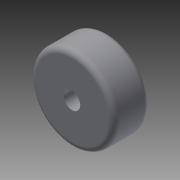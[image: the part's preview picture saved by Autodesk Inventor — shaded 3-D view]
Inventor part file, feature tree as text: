
AUTODESK INVENTOR PART (.ipt)
format: ipt  version: 2013 (Build 170138000, 138)  size: 110,592 bytes
history: native  units: in
note: dims shown in document units (in); Inventor stores cm internally (conversion verified against a paired STEP export)
features: extrude x2, sketch x2, fillet x1
ambient origin geometry x8: Origin, YZ Plane, XZ Plane, XY Plane, X Axis, Y Axis, Z Axis, Center Point
bodies: Solid1 (feature_tree)
feature tree (5):
  extrude  "Extrusion1"  Depth=0.8125in TaperAngle=0.0deg
  extrude  "Extrusion2"  Depth=0.5in TaperAngle=0.0deg
  fillet  "Fillet1"  Radius=0.125in
  sketch  "Sketch1"  dims[d0=1.875in d1=0.8125in d2=0.0in]
  sketch  "Sketch2"  dims[d3=0.375in d4=0.5in d5=0.0in d6=0.125in]
